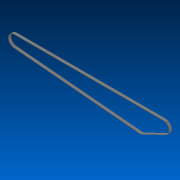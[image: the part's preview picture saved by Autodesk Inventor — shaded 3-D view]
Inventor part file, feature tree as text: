
AUTODESK INVENTOR PART (.ipt)
format: ipt  version: 2022 (Build 260153000, 153)  size: 107,008 bytes
history: native  units: in
note: dims shown in document units (in); Inventor stores cm internally (conversion verified against a paired STEP export)
features: extrude x1, sketch x1
ambient origin geometry x8: Origin, YZ Plane, XZ Plane, XY Plane, X Axis, Y Axis, Z Axis, Center Point
bodies: Solid1 (feature_tree)
feature tree (2):
  extrude  "Extrusion1"  Depth=0.3543in
  sketch  "Sketch1"  dims[d0=19.5in d1=1.504in d2=0.0394in d3=0.3543in d4=0.0in d5=0.875in d6=3.0in d7=1.8in]
